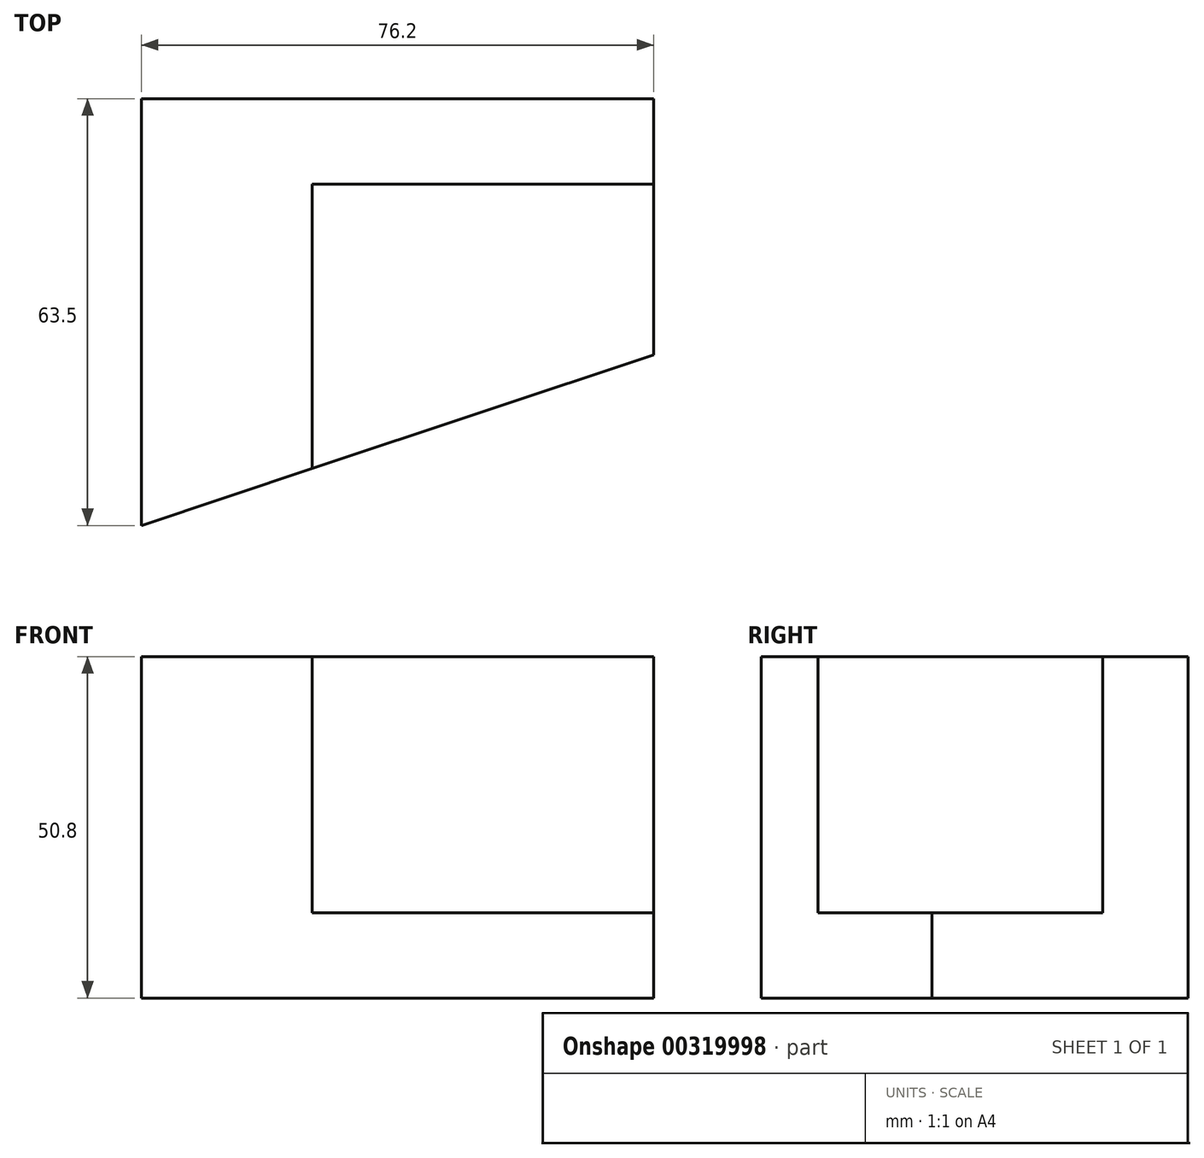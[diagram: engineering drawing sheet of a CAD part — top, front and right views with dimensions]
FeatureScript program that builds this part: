
annotation { "Feature Type Name" : "Feature", "Feature Type Description" : "" }
export const myFeature = defineFeature(function(context is Context, id is Id, definition is map)
    precondition{}
    {
        {
            var Q0;
            Q0=qCreatedBy(makeId("Front.planeOp"),FACE);
            var sketch = newSketch(context, id + "F0", { "sketchPlane" : qUnion([Q0])});
            skLineSegment(sketch, "E0", {"start": v(0, 0) * mm, "end": v(76.2, 0) * mm});
            skLineSegment(sketch, "E1", {"start": v(76.2, 0) * mm, "end": v(76.2, 50.8) * mm});
            skLineSegment(sketch, "E2", {"start": v(76.2, 50.8) * mm, "end": v(0, 50.8) * mm});
            skLineSegment(sketch, "E3", {"start": v(0, 50.8) * mm, "end": v(0, 0) * mm});
            skLineSegment(sketch, "E4", {"start": v(25.4, 50.8) * mm, "end": v(25.4, 12.7) * mm});
            skLineSegment(sketch, "E5", {"start": v(25.4, 12.7) * mm, "end": v(76.2, 12.7) * mm});
            skSolve(sketch);
        }
        {
            var Q0;
            Q0 = qSketchRegion(id + "F0", true);
            extrude(context, id + "F1", {"entities" : qUnion([Q0]), "oppositeDirection" : true, "depth" : 63.5 * mm});
        }
        {
            var Q0;
            Q0=makeQuery(id+"F1.opExtrude","SWEPT_FACE",FACE,{"disambiguationData":[OSD([sQuery(id+"F0.wireOp",EDGE,"E2")])]});
            var sketch = newSketch(context, id + "F2", { "sketchPlane" : qUnion([Q0])});
            skLineSegment(sketch, "E6", {"start": v(0, 0) * mm, "end": v(76.2, 25.4) * mm});
            skLineSegment(sketch, "E7", {"start": v(25.4, 8.47) * mm, "end": v(25.4, 50.8) * mm});
            skLineSegment(sketch, "E8", {"start": v(25.4, 50.8) * mm, "end": v(76.2, 50.8) * mm});
            skSolve(sketch);
        }
        {
            var Q0;
            {var subQ1=sQuery(id+"F0.wireOp",EDGE,"E2");var subQ2=makeQuery(id+"F1.opExtrude","CAP_EDGE",EDGE,{"disambiguationData":[OSD([subQ1])],"isStart":true});Q0=makeQuery(id+"F2.imprint","IMPRINT",FACE,{"disambiguationData":[TD([[makeQuery(id+"F2.imprint","IMPRINT",EDGE,{"derivedFrom":subQ2}),-1.0]])]});}
            extrude(context, id + "F3", {"entities" : qUnion([Q0]), "operationType" : NewBodyOperationType.REMOVE, "endBound" : BoundingType.THROUGH_ALL, "oppositeDirection" : true, "depth" : 25.4 * mm});
        }
        {
            var Q0;
            {var subQ3=sQuery(id+"F2.wireOp",EDGE,"E7");Q0=makeQuery(id+"F2.imprint","IMPRINT",FACE,{"disambiguationData":[TD([[makeQuery(id+"F2.imprint","IMPRINT",EDGE,{"derivedFrom":subQ3}),-1.0]])]});}
            extrude(context, id + "F4", {"entities" : qUnion([Q0]), "operationType" : NewBodyOperationType.REMOVE, "oppositeDirection" : true, "depth" : 38.1 * mm});
        }
    });
